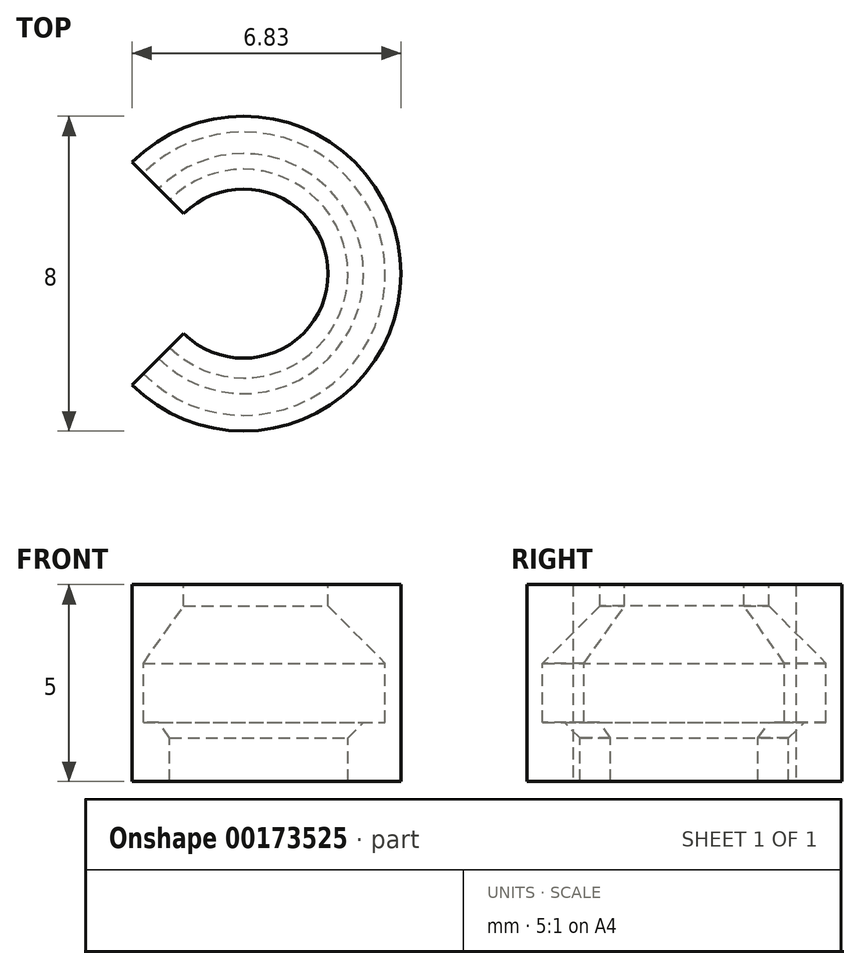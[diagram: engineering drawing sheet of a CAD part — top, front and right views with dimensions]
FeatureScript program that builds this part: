
annotation { "Feature Type Name" : "Feature", "Feature Type Description" : "" }
export const myFeature = defineFeature(function(context is Context, id is Id, definition is map)
    precondition{}
    {
        {
            var Q0;
            Q0=qCreatedBy(makeId("Front.planeOp"),FACE);
            var sketch = newSketch(context, id + "F0", { "sketchPlane" : qUnion([Q0])});
            skLineSegment(sketch, "E0", {"start": v(2.65, 0) * mm, "end": v(2.65, 1.5) * mm});
            skLineSegment(sketch, "E1", {"start": v(2.65, 1.5) * mm, "end": v(3.6, 1.5) * mm});
            skLineSegment(sketch, "E2", {"start": v(3.6, 1.5) * mm, "end": v(3.6, 3) * mm});
            skLineSegment(sketch, "E3", {"start": v(3.6, 3) * mm, "end": v(2.15, 3) * mm});
            skLineSegment(sketch, "E4", {"start": v(2.15, 3) * mm, "end": v(2.15, 5) * mm});
            skLineSegment(sketch, "E5", {"start": v(2.15, 5) * mm, "end": v(4, 5) * mm});
            skLineSegment(sketch, "E6", {"start": v(4, 5) * mm, "end": v(4, 0) * mm});
            skLineSegment(sketch, "E7", {"start": v(4, 0) * mm, "end": v(2.65, 0) * mm});
            skLineSegment(sketch, "E8", {"start": v(0, 5) * mm, "end": v(0, 0) * mm, "construction": true});
            skSolve(sketch);
        }
        {
            var Q0;
            Q0 = qSketchRegion(id + "F0", true);
            var Q1;
            Q1=sQuery(id+"F0.wireOp",EDGE,"E8");
            revolve(context, id + "F1", {"entities" : qUnion([Q0]), "axis" : qUnion([Q1]), "revolveType" : RevolveType.SYMMETRIC, "angle" : 270 * degree});
        }
        {
            var Q0;
            Q0=makeQuery(id+"F1.opRevolve","SWEPT_EDGE",EDGE,{"disambiguationData":[OSD([sQuery(id+"F0.wireOp",EDGE,"E0"),sQuery(id+"F0.wireOp",EDGE,"E1")])]});
            chamfer(context, id + "F2", {"entities" : qUnion([Q0]), "width" : 0.4 * mm, "tangentPropagation" : true});
        }
        {
            var Q0;
            Q0=makeQuery(id+"F1.opRevolve","SWEPT_EDGE",EDGE,{"disambiguationData":[OSD([sQuery(id+"F0.wireOp",EDGE,"E3"),sQuery(id+"F0.wireOp",EDGE,"E4")])]});
            chamfer(context, id + "F3", {"entities" : qUnion([Q0]), "width" : 1.45 * mm, "tangentPropagation" : true});
        }
    });
